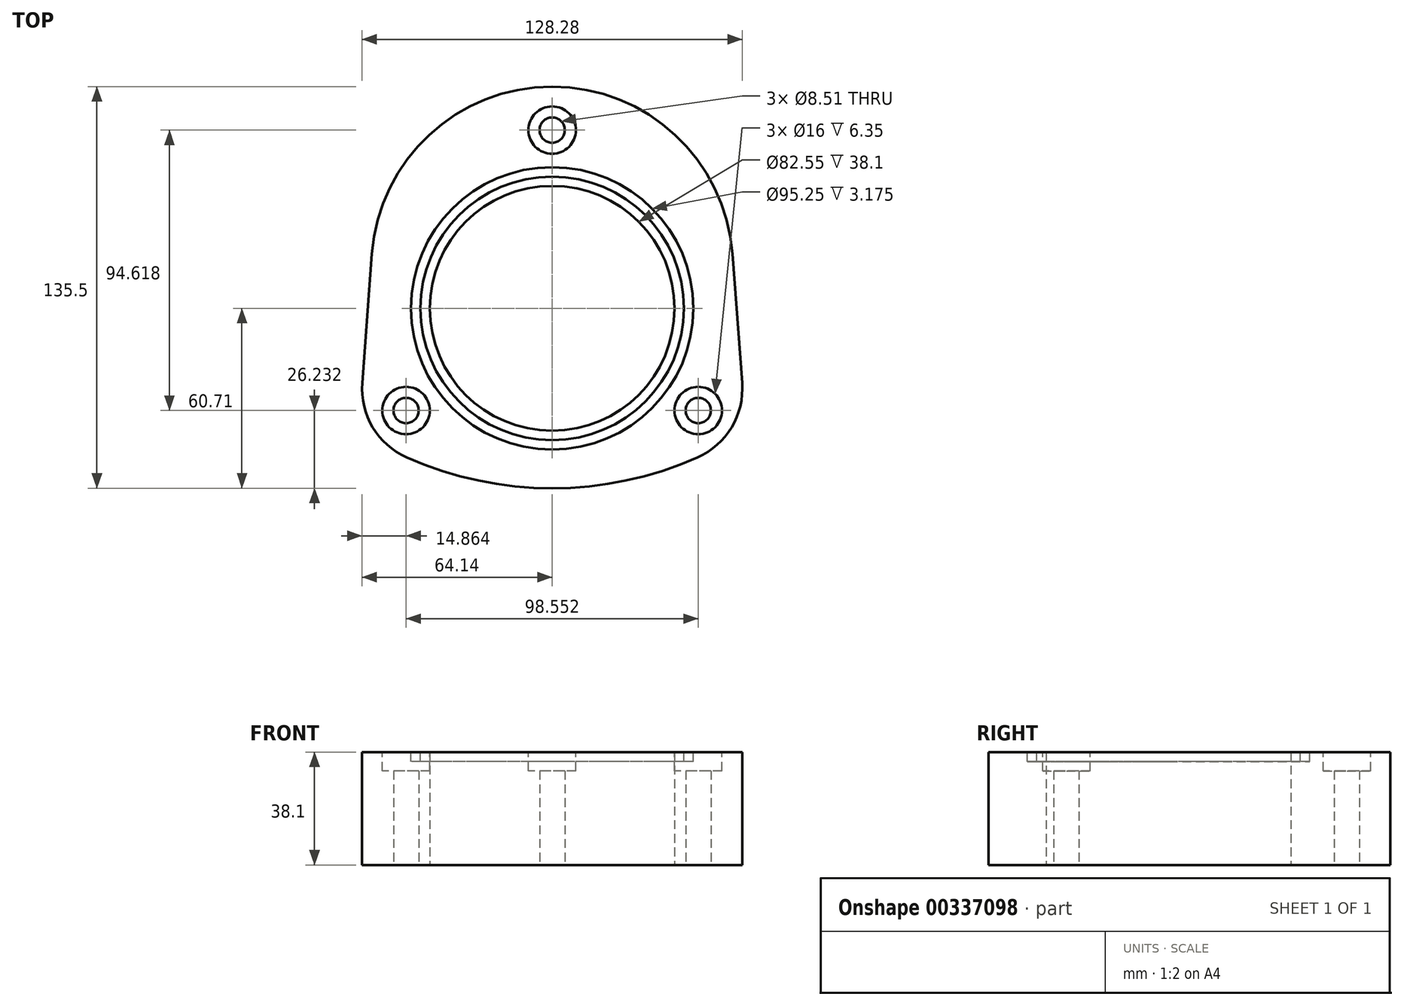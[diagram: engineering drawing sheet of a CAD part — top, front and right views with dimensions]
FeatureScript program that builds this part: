
annotation { "Feature Type Name" : "Feature", "Feature Type Description" : "" }
export const myFeature = defineFeature(function(context is Context, id is Id, definition is map)
    precondition{}
    {
        {
            var Q0;
            Q0=qCreatedBy(makeId("Top.planeOp"),FACE);
            var sketch = newSketch(context, id + "F0", { "sketchPlane" : qUnion([Q0])});
            skCircle(sketch, "E0", {"center": v(0, 0) * mm, "radius": 41.28 * mm});
            skCircle(sketch, "E1", {"center": v(0, 60.14) * mm, "radius": 4.25 * mm});
            skCircle(sketch, "E2", {"center": v(-49.28, -34.48) * mm, "radius": 4.25 * mm});
            skCircle(sketch, "E3", {"center": v(49.28, -34.48) * mm, "radius": 4.25 * mm});
            skLineSegment(sketch, "E4", {"start": v(0, 60.14) * mm, "end": v(-49.28, -34.48) * mm, "construction": true});
            skLineSegment(sketch, "E5", {"start": v(0, 60.14) * mm, "end": v(49.28, -34.48) * mm, "construction": true});
            skLineSegment(sketch, "E6", {"start": v(49.28, -34.48) * mm, "end": v(-49.28, -34.48) * mm, "construction": true});
            skLineSegment(sketch, "E7", {"start": v(0, 60.14) * mm, "end": v(0, -34.48) * mm, "construction": true});
            skLineSegment(sketch, "E8", {"start": v(-24.64, 12.83) * mm, "end": v(7.73, -4.02) * mm, "construction": true});
            skLineSegment(sketch, "E9", {"start": v(24.64, 12.83) * mm, "end": v(-9.71, -5.06) * mm, "construction": true});
            skArc(sketch, "E10", {"start": v(60.79, 18.4) * mm, "mid": v(0, 74.8) * mm, "end": v(-60.79, 18.4) * mm});
            skArc(sketch, "E11", {"start": v(-64.06, -25.2) * mm, "mid": v(-60.53, -40.14) * mm, "end": v(-49.04, -50.32) * mm});
            skArc(sketch, "E12", {"start": v(49.04, -50.32) * mm, "mid": v(60.53, -40.14) * mm, "end": v(64.06, -25.2) * mm});
            skArc(sketch, "E13", {"start": v(-49.04, -50.32) * mm, "mid": v(0, -60.71) * mm, "end": v(49.04, -50.32) * mm});
            skLineSegment(sketch, "E14", {"start": v(-67.64, 74.8) * mm, "end": v(73.45, 74.8) * mm, "construction": true});
            skLineSegment(sketch, "E15", {"start": v(-66.47, -60.71) * mm, "end": v(67.57, -60.71) * mm, "construction": true});
            skLineSegment(sketch, "E16", {"start": v(-64.13, 55.37) * mm, "end": v(-64.13, -47.17) * mm, "construction": true});
            skLineSegment(sketch, "E17", {"start": v(64.14, 64.96) * mm, "end": v(64.14, -44.23) * mm, "construction": true});
            skLineSegment(sketch, "E18", {"start": v(-49.28, -34.48) * mm, "end": v(0, 0) * mm, "construction": true});
            skLineSegment(sketch, "E19", {"start": v(49.28, -34.48) * mm, "end": v(0, 0) * mm, "construction": true});
            skLineSegment(sketch, "E20", {"start": v(-60.79, 18.4) * mm, "end": v(-64.06, -25.2) * mm});
            skLineSegment(sketch, "E21", {"start": v(60.79, 18.4) * mm, "end": v(64.06, -25.2) * mm});
            skLineSegment(sketch, "E22", {"start": v(-22.09, 0) * mm, "end": v(21.01, 0) * mm, "construction": true});
            skSolve(sketch);
        }
        {
            var Q0;
            Q0=makeQuery(id+"F0.imprint","IMPRINT",FACE,{"disambiguationData":[TD([[makeQuery(id+"F0.imprint","IMPRINT",EDGE,{"derivedFrom":sQuery(id+"F0.wireOp",EDGE,"E0")}),-1.0]])]});
            extrude(context, id + "F1", {"entities" : qUnion([Q0]), "depth" : 38.1 * mm});
        }
        {
            var Q0;
            Q0=makeQuery(id+"F1.opExtrude","CAP_FACE",FACE,{"disambiguationData":[OSD([sQuery(id+"F0.wireOp",EDGE,"E0"),sQuery(id+"F0.wireOp",EDGE,"E1"),sQuery(id+"F0.wireOp",EDGE,"E2"),sQuery(id+"F0.wireOp",EDGE,"E3"),sQuery(id+"F0.wireOp",EDGE,"E10"),sQuery(id+"F0.wireOp",EDGE,"E11"),sQuery(id+"F0.wireOp",EDGE,"E12"),sQuery(id+"F0.wireOp",EDGE,"E13"),sQuery(id+"F0.wireOp",EDGE,"E20"),sQuery(id+"F0.wireOp",EDGE,"E21")])],"isStart":false});
            var sketch = newSketch(context, id + "F2", { "sketchPlane" : qUnion([Q0])});
            skCircle(sketch, "E23", {"center": v(0, 60.14) * mm, "radius": 8 * mm});
            skCircle(sketch, "E24", {"center": v(49.28, -34.48) * mm, "radius": 8 * mm});
            skCircle(sketch, "E25", {"center": v(-49.28, -34.48) * mm, "radius": 8 * mm});
            skCircle(sketch, "E26", {"center": v(0, 0) * mm, "radius": 44.45 * mm});
            skCircle(sketch, "E27", {"center": v(0, 0) * mm, "radius": 47.63 * mm});
            skSolve(sketch);
        }
        {
            var Q0;
            Q0=makeQuery(id+"F2.imprint","IMPRINT",FACE,{"disambiguationData":[TD([[makeQuery(id+"F2.imprint","IMPRINT",EDGE,{"derivedFrom":sQuery(id+"F2.wireOp",EDGE,"E23")}),1.0]])]});
            var Q1;
            Q1=makeQuery(id+"F2.imprint","IMPRINT",FACE,{"disambiguationData":[TD([[makeQuery(id+"F2.imprint","IMPRINT",EDGE,{"derivedFrom":sQuery(id+"F2.wireOp",EDGE,"E25")}),1.0]])]});
            var Q2;
            Q2=makeQuery(id+"F2.imprint","IMPRINT",FACE,{"disambiguationData":[TD([[makeQuery(id+"F2.imprint","IMPRINT",EDGE,{"derivedFrom":sQuery(id+"F2.wireOp",EDGE,"E24")}),1.0]])]});
            extrude(context, id + "F3", {"entities" : qUnion([Q0, Q1, Q2]), "operationType" : NewBodyOperationType.REMOVE, "oppositeDirection" : true, "depth" : 6.35 * mm});
        }
        {
            var Q0;
            Q0=makeQuery(id+"F2.imprint","IMPRINT",FACE,{"disambiguationData":[TD([[makeQuery(id+"F2.imprint","IMPRINT",EDGE,{"derivedFrom":sQuery(id+"F2.wireOp",EDGE,"E26")}),-1.0]])]});
            extrude(context, id + "F4", {"entities" : qUnion([Q0]), "operationType" : NewBodyOperationType.REMOVE, "oppositeDirection" : true, "depth" : 3.17 * mm});
        }
    });
